# Revit family: Pump station MAGMAmodule® Fresh Mini (2021)
name_source: partatom
category: Mechanical Equipment
units: mm (PartAtom-declared; Revit-internal decimal feet)

## family parameters
Always vertical = Yes
Classification = Pump
Cut with Voids When Loaded = No
OmniClass Number = 23.75.00.00
OmniClass Title = Climate Control (HVAC)
Part Type = Normal
Room Calculation Point = No
Round Connector Dimension = Use Diameter
Shared = Yes
Work Plane-Based = No

## types (1)
- Pump station MAGMAmodule® Fresh Mini (2021)
    Assembly Code = F012040R
    Data revision = 21.02.2024
    Default Elevation = 1400 mm  [stored 4.59318 ft]
    Description = Автоматична станція гарячого водопостачання MAGMAmodule® Fresh Mini з продуктивністю до 40 л/хв, доступна в конфігурації:

R – інтегрований вузол рециркуляції ГВП з керуванням по температурі і часу (станція без вузла рециркуляції тільки по замовленню).
Станція нагріває воду у проточному режимі за рахунок теплової енергії, яка накопичується у буфері за рахунок будь-яких теплогенераторів – газовий котел, електричний котел, тепловий насос і т.д.

Кожен модуль за запитом може оснащуватися системою дистанційного моніторингу та управління KM2
    Model = MAGMAmodule® Fresh Mini
    Revit/family revision = revit-2021/family-1.1
    Type Image = magmamodule-fresh-front.jpg
    URL = https://www.magmaenergy.com.ua
    YouTube = https://www.youtube.com
    d1_Т3 = 20 mm  [stored 0.0656168 ft]
    d2_Т4 = 20 mm  [stored 0.0656168 ft]
    d3_В1 = 20 mm  [stored 0.0656168 ft]
    d4_Т1 = 20 mm  [stored 0.0656168 ft]
    d5_Т2 = 20 mm  [stored 0.0656168 ft]
    r1 = 10 mm  [stored 0.0328084 ft]
    r2 = 10 mm  [stored 0.0328084 ft]
    r3 = 10 mm  [stored 0.0328084 ft]
    r4 = 10 mm  [stored 0.0328084 ft]
    r5 = 10 mm  [stored 0.0328084 ft]
    Напруга = 230 В
    Споживана потужність = 150 Вт
    Струм = 1 А

note: [stored X ft] marks values corroborated as IEEE doubles in the binary element streams (Revit-internal decimal feet)

## geometry (parser evidence)
native form markers: Sweep x3
no freeform markers — native parametric forms only
